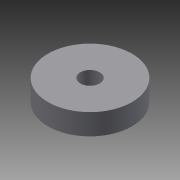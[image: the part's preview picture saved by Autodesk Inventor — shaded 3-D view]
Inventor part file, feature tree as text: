
AUTODESK INVENTOR PART (.ipt)
format: ipt  version: 2013 (Build 170138000, 138)  size: 79,872 bytes
history: native  units: mm
features: extrude x1, sketch x1
ambient origin geometry x8: Origin, YZ Plane, XZ Plane, XY Plane, X Axis, Y Axis, Z Axis, Center Point
feature tree (2):
  extrude  "Extrusion5"  Depth=3.0mm
  sketch  "Sketch1"  dims[d3=3.0mm d5=3.0mm d35=13.0mm d36=3.0mm d37=3.25mm d38=0.0mm]
